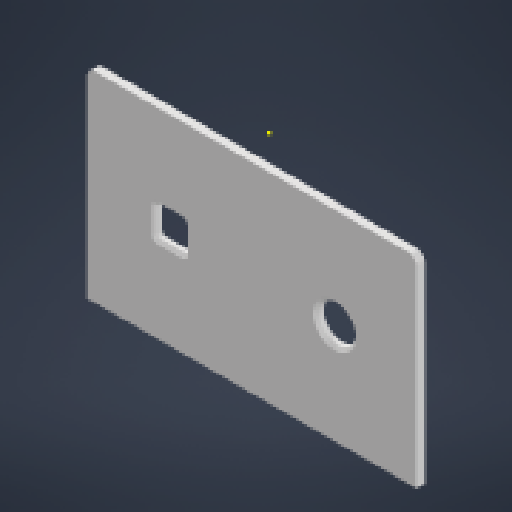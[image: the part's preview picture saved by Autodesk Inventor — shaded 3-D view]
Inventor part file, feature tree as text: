
AUTODESK INVENTOR PART (.ipt)
format: ipt  version: 2024.2 (Build 282272000, 272)  size: 412,672 bytes
history: native  units: mm
features: sketch x3, extrude x2, fillet x2, other x1, projected_geometry x1
ambient origin geometry x8: Origin, YZ Plane, XZ Plane, XY Plane, X Axis, Y Axis, Z Axis, Center Point
bodies: Body1 (feature_tree)
feature tree (9):
  other  "솔리드1"
  extrude  "돌출1"  Depth=207.0mm
  sketch  "스케치2"
  extrude  "돌출3"  Depth=126.0mm
  fillet  "모깎기4"  Radius=5.0mm
  fillet  "모깎기5"  Radius=5.0mm
  sketch  "스케치1"
  sketch  "스케치4"
  projected_geometry  "투영된 루프1"
